# Revit family: TD92_OCA709_AMA000_RVT20_R00
name_source: partatom
category: Mobiliário
units: mm (PartAtom-declared; Revit-internal decimal feet)

## family parameters
Com base no plano de trabalho = Não
Compartilhado = Não
Corte com vazios quando carregada = Não
Número OmniClass = 23.40.20.00
Ponto de cálculo do ambiente = Não
Sempre na vertical = Sim
Título OmniClass = General Furniture and Specialties

## types (1)
- TD92_OCA709_AMA000_RVT20_R00
    Descrição = Deixe os momentos e os ambientes das crianças mais alegres e divertidos com a Poltrona Oca Infantil Tramontina em Polietileno. Com design criativo e descontraído, ela é produzida em material livre de toxinas e vai garantir maior bem-estar e conforto, além de compor perfeitamente o quarto dos pequenos ou playgrounds de casas ou condomínios. Sua cor é vibrante e chamará a atenção de todos!
    Elevação padrão = 0  [stored 0 ft]
    Fabricante = Tramontina Delta S/A
    Modelo = Poltrona Oca Infantil Tramontina em Polietileno Amarelo
    Nota-chave = 92709000
    URL = https://www.tramontinastore.com

note: [stored X ft] marks values corroborated as IEEE doubles in the binary element streams (Revit-internal decimal feet)
